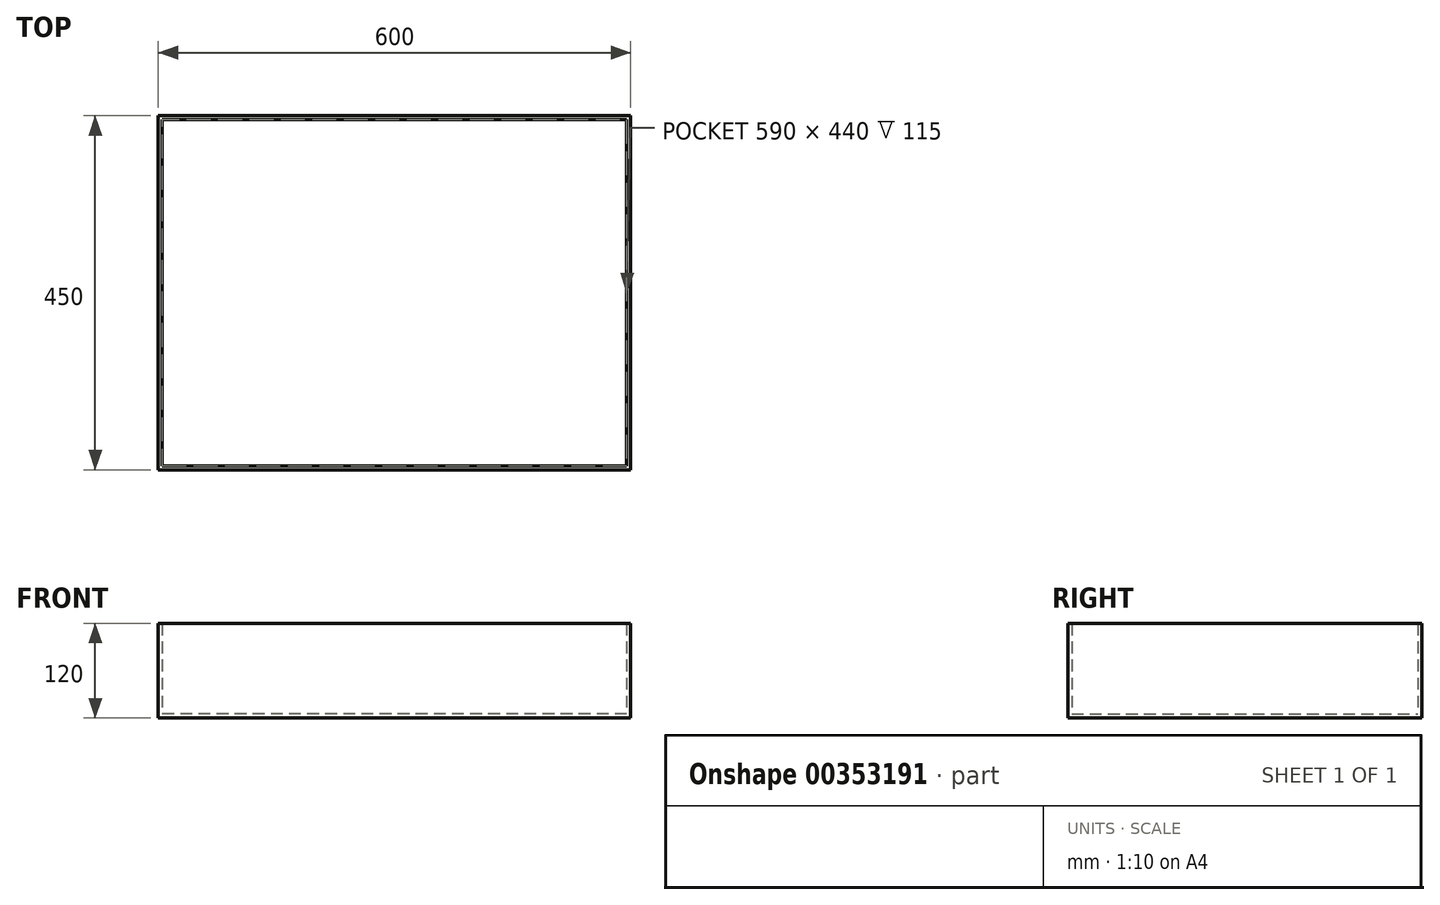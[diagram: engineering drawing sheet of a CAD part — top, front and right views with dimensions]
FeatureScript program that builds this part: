
annotation { "Feature Type Name" : "Feature", "Feature Type Description" : "" }
export const myFeature = defineFeature(function(context is Context, id is Id, definition is map)
    precondition{}
    {
        {
            var Q0;
            Q0=qCreatedBy(makeId("Top.planeOp"),FACE);
            var sketch = newSketch(context, id + "F0", { "sketchPlane" : qUnion([Q0])});
            skLineSegment(sketch, "E0.bottom", {"start": v(-37.37, 432.63) * mm, "end": v(562.63, 432.63) * mm});
            skLineSegment(sketch, "E0.top", {"start": v(-37.37, -17.37) * mm, "end": v(562.63, -17.37) * mm});
            skLineSegment(sketch, "E0.left", {"start": v(-37.37, 432.63) * mm, "end": v(-37.37, -17.37) * mm});
            skLineSegment(sketch, "E0.right", {"start": v(562.63, 432.63) * mm, "end": v(562.63, -17.37) * mm});
            skLineSegment(sketch, "E1.0", {"start": v(-32.37, 427.63) * mm, "end": v(557.63, 427.63) * mm});
            skLineSegment(sketch, "E1.1", {"start": v(-32.37, 427.63) * mm, "end": v(-32.37, -12.37) * mm});
            skLineSegment(sketch, "E1.2", {"start": v(-32.37, -12.37) * mm, "end": v(557.63, -12.37) * mm});
            skLineSegment(sketch, "E1.3", {"start": v(557.63, 427.63) * mm, "end": v(557.63, -12.37) * mm});
            skSolve(sketch);
        }
        {
            var Q0;
            Q0=makeQuery(id+"F0.imprint","IMPRINT",FACE,{"disambiguationData":[TD([[makeQuery(id+"F0.imprint","IMPRINT",EDGE,{"derivedFrom":sQuery(id+"F0.wireOp",EDGE,"E0.bottom")}),-1.0]])]});
            extrude(context, id + "F1", {"entities" : qUnion([Q0]), "depth" : 120 * mm});
        }
        {
            var Q0;
            Q0=makeQuery(id+"F1.opExtrude","CAP_FACE",FACE,{"disambiguationData":[OSD([sQuery(id+"F0.wireOp",EDGE,"E0.bottom"),sQuery(id+"F0.wireOp",EDGE,"E0.top"),sQuery(id+"F0.wireOp",EDGE,"E0.left"),sQuery(id+"F0.wireOp",EDGE,"E0.right"),sQuery(id+"F0.wireOp",EDGE,"E1.0"),sQuery(id+"F0.wireOp",EDGE,"E1.1"),sQuery(id+"F0.wireOp",EDGE,"E1.2"),sQuery(id+"F0.wireOp",EDGE,"E1.3")])],"isStart":true});
            var sketch = newSketch(context, id + "F2", { "sketchPlane" : qUnion([Q0])});
            skLineSegment(sketch, "E2.bottom", {"start": v(-37.37, 17.37) * mm, "end": v(562.63, 17.37) * mm});
            skLineSegment(sketch, "E2.top", {"start": v(-37.37, -432.63) * mm, "end": v(562.63, -432.63) * mm});
            skLineSegment(sketch, "E2.left", {"start": v(-37.37, 17.37) * mm, "end": v(-37.37, -432.63) * mm});
            skLineSegment(sketch, "E2.right", {"start": v(562.63, 17.37) * mm, "end": v(562.63, -432.63) * mm});
            skSolve(sketch);
        }
        {
            var Q0;
            Q0 = qSketchRegion(id + "F2", true);
            extrude(context, id + "F3", {"entities" : qUnion([Q0]), "operationType" : NewBodyOperationType.ADD, "oppositeDirection" : true, "depth" : 5 * mm});
        }
    });
